# Revit family: heroal W 72 i CW Double Window
name_source: partatom
category: Fenster
revit_build: Autodesk Revit 2017 (Build: 20160225_1515(x64)
units: mm (PartAtom-declared; Revit-internal decimal feet)

## family parameters
Beim Laden mit Abzugskörper schneiden = Nein
Gemeinsam genutzt = Nein
Immer vertikal = Ja
OmniClass-Nummer = 23.30.20.00
OmniClass-Titel = Windows
Raumberechnungspunkt = Ja

## types (1)
- heroal W 72 i CW Double Window
    Ability To Bear Safety Equipment DIN EN 14351 = Fullfilled
    Air Permeability DIN EN 12207 = 4
    Analytische Konstruktion = <None>
    Baugruppenkennzeichen = B2020110
    Beschreibung = heroal W 72 i Aluminium Window Systems
    Burglary Resistance DIN V ENV 1627 = RC1-RC2
    Continuous Function DIN EN 12400 = 3
    Edition number = 2
    Heat Insulation [Uf in W/m2K] DIN EN ISO 10077 = 1.5
    Heat Insulation [Uf in W/m2K]/Standard Profile View DIN EN ISO 10077 = 1.5/97
    Heat Insulation [Uw in W/m2K] DIN EN ISO 10077-1 = ≥0.84
    Hersteller = heroal
    Leaf Type 1 = Leaf : Bottom-Hung
    Leaf Type 2 = Leaf : Fixed
    Leaf Type 3 = Leaf : Side-Hung
    Leaf Type 4 = Leaf : Tilt and Turn
    Max. Casement Leaf Height = 2400mm
    Max. Casement Weight = 150kg
    Max. Thickness Of Glass/Infill Panel = Frame 52mm / Casement 47mm
    Mechanical Durability DIN EN 13115 = 4
    Modell = heroal W 72 i 60/i33
    Operating forces DIN EN 12217 = 1
    Profile Installation Depth - Casement Profiles = 76.5mm
    Profile Installation Depth - Cross Bar Profiles = 72mm
    Profile Installation Depth - Frame Profiles = 72mm
    Profile View Width - Casement Profiles = Hidden
    Profile View Width - Cross Bar Profiles = 114-244mm
    Profile View Width - Frame Profiles = 70-120mm
    Shock Resistance DIN EN 13049 = 4
    Soundproofing Class DIN EN ISO 717-1 = 1-5
    Tightness Against Driving Rain DIN EN 12208 = 9A
    URL = http://www.heroal.com
    Wind Load Resistance DIN EN 12210 = C5/B5

## geometry (parser evidence)
native form markers: Blend x1, Sweep x13
no freeform markers — native parametric forms only
